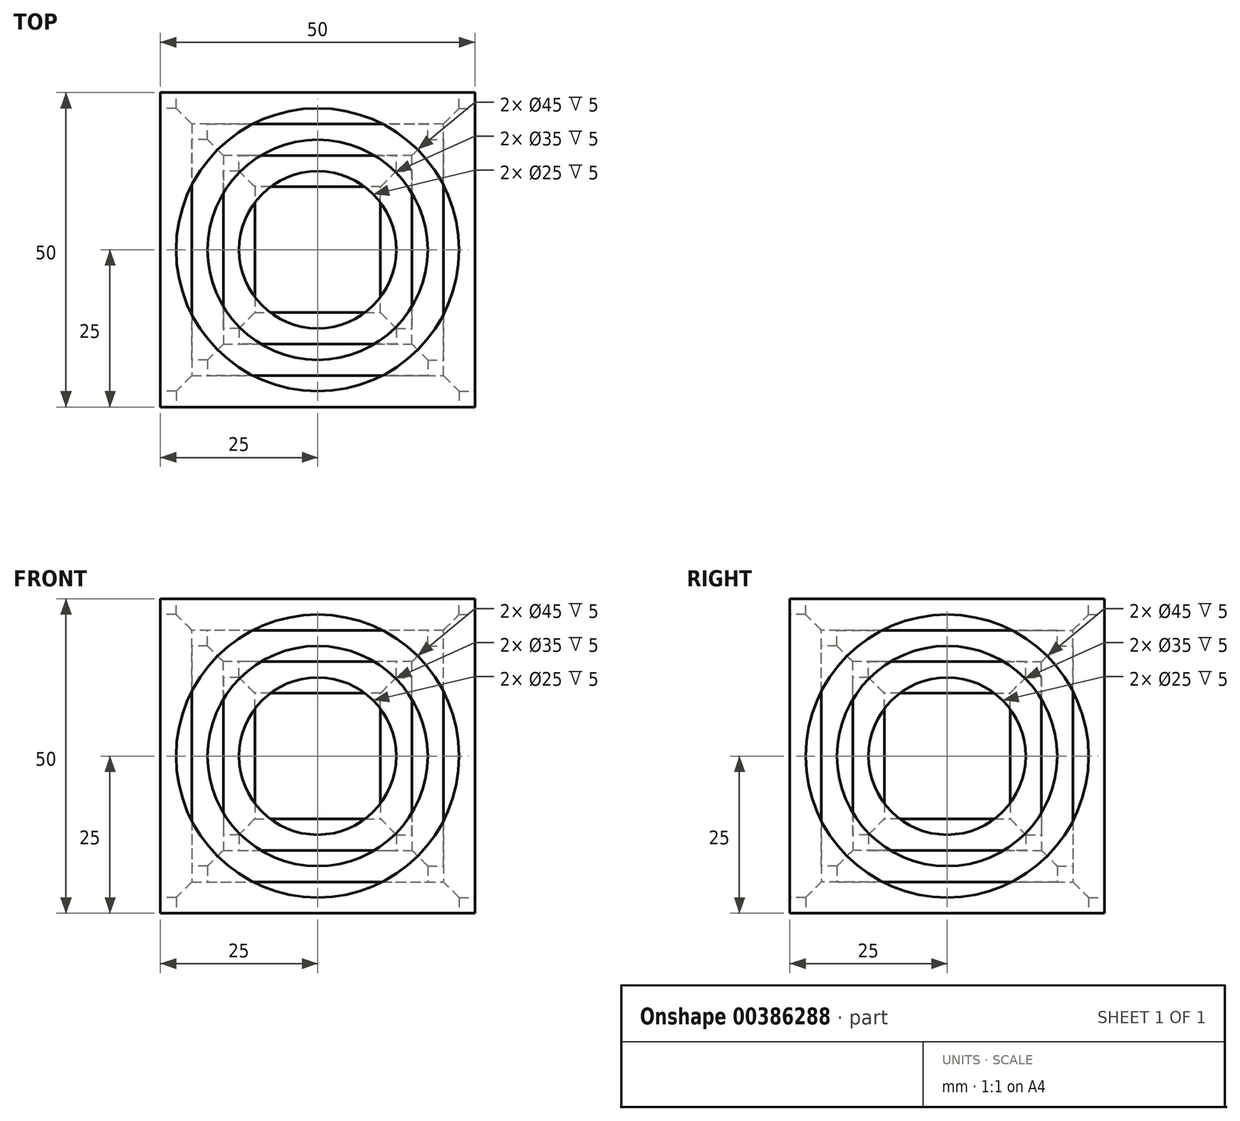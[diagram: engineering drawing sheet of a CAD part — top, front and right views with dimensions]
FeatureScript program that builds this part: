
annotation { "Feature Type Name" : "Feature", "Feature Type Description" : "" }
export const myFeature = defineFeature(function(context is Context, id is Id, definition is map)
    precondition{}
    {
        {
            var Q0;
            Q0=qCreatedBy(makeId("Top.planeOp"),FACE);
            var sketch = newSketch(context, id + "F0", { "sketchPlane" : qUnion([Q0])});
            skLineSegment(sketch, "E0.bottom", {"start": v(0, 0) * mm, "end": v(50, 0) * mm});
            skLineSegment(sketch, "E0.top", {"start": v(0, 50) * mm, "end": v(50, 50) * mm});
            skLineSegment(sketch, "E0.left", {"start": v(0, 0) * mm, "end": v(0, 50) * mm});
            skLineSegment(sketch, "E0.right", {"start": v(50, 0) * mm, "end": v(50, 50) * mm});
            skSolve(sketch);
        }
        {
            var Q0;
            Q0=makeQuery(id+"F0.imprint","IMPRINT",FACE,{"disambiguationData":[TD([[makeQuery(id+"F0.imprint","IMPRINT",EDGE,{"derivedFrom":sQuery(id+"F0.wireOp",EDGE,"E0.bottom")}),1.0]])]});
            extrude(context, id + "F1", {"entities" : qUnion([Q0]), "depth" : 50 * mm});
        }
        {
            var Q0;
            Q0=makeQuery(id+"F1.opExtrude","CAP_FACE",FACE,{"disambiguationData":[OSD([sQuery(id+"F0.wireOp",EDGE,"E0.bottom"),sQuery(id+"F0.wireOp",EDGE,"E0.top"),sQuery(id+"F0.wireOp",EDGE,"E0.left"),sQuery(id+"F0.wireOp",EDGE,"E0.right")])],"isStart":false});
            var sketch = newSketch(context, id + "F2", { "sketchPlane" : qUnion([Q0])});
            skCircle(sketch, "E1", {"center": v(25, 25) * mm, "radius": 22.5 * mm});
            skPoint(sketch, "E1.centerSnap0", {"position": v(50, 25) * mm});
            skPoint(sketch, "E1.centerSnap1", {"position": v(25, 50) * mm});
            skSolve(sketch);
        }
        {
            var Q0;
            Q0=makeQuery(id+"F2.imprint","IMPRINT",FACE,{"disambiguationData":[TD([[makeQuery(id+"F2.imprint","IMPRINT",EDGE,{"derivedFrom":sQuery(id+"F2.wireOp",EDGE,"E1")}),1.0]])]});
            extrude(context, id + "F3", {"entities" : qUnion([Q0]), "operationType" : NewBodyOperationType.REMOVE, "oppositeDirection" : true, "depth" : 5 * mm});
        }
        {
            var Q0;
            Q0=makeQuery(id+"F3.boolean.opBoolean","COPY",FACE,{"derivedFrom":makeQuery(id+"F3.opExtrude","CAP_FACE",FACE,{"disambiguationData":[OSD([sQuery(id+"F2.wireOp",EDGE,"E1")])],"isStart":false})});
            var sketch = newSketch(context, id + "F4", { "sketchPlane" : qUnion([Q0])});
            skCircle(sketch, "E2", {"center": v(25, 25) * mm, "radius": 17.5 * mm});
            skSolve(sketch);
        }
        {
            var Q0;
            Q0=makeQuery(id+"F4.imprint","IMPRINT",FACE,{"disambiguationData":[TD([[makeQuery(id+"F4.imprint","IMPRINT",EDGE,{"derivedFrom":sQuery(id+"F4.wireOp",EDGE,"E2")}),1.0]])]});
            extrude(context, id + "F5", {"entities" : qUnion([Q0]), "operationType" : NewBodyOperationType.REMOVE, "oppositeDirection" : true, "depth" : 5 * mm});
        }
        {
            var Q0;
            Q0=makeQuery(id+"F5.boolean.opBoolean","COPY",FACE,{"derivedFrom":makeQuery(id+"F5.opExtrude","CAP_FACE",FACE,{"disambiguationData":[OSD([sQuery(id+"F4.wireOp",EDGE,"E2")])],"isStart":false})});
            var sketch = newSketch(context, id + "F6", { "sketchPlane" : qUnion([Q0])});
            skCircle(sketch, "E3", {"center": v(25, 25) * mm, "radius": 12.5 * mm});
            skSolve(sketch);
        }
        {
            var Q0;
            Q0 = qSketchRegion(id + "F6", true);
            extrude(context, id + "F7", {"entities" : qUnion([Q0]), "operationType" : NewBodyOperationType.REMOVE, "oppositeDirection" : true, "depth" : 5 * mm});
        }
        {
            var Q0;
            Q0=makeQuery(id+"F1.opExtrude","SWEPT_FACE",FACE,{"disambiguationData":[OSD([sQuery(id+"F0.wireOp",EDGE,"E0.left")])]});
            var sketch = newSketch(context, id + "F8", { "sketchPlane" : qUnion([Q0])});
            skCircle(sketch, "E4", {"center": v(-25, 25) * mm, "radius": 22.5 * mm});
            skPoint(sketch, "E4.centerSnap0", {"position": v(-25, 50) * mm});
            skPoint(sketch, "E4.centerSnap1", {"position": v(-50, 25) * mm});
            skSolve(sketch);
        }
        {
            var Q0;
            Q0=makeQuery(id+"F8.imprint","IMPRINT",FACE,{"disambiguationData":[TD([[makeQuery(id+"F8.imprint","IMPRINT",EDGE,{"derivedFrom":sQuery(id+"F8.wireOp",EDGE,"E4")}),1.0]])]});
            extrude(context, id + "F9", {"entities" : qUnion([Q0]), "operationType" : NewBodyOperationType.REMOVE, "oppositeDirection" : true, "depth" : 5 * mm});
        }
        {
            var Q0;
            Q0=makeQuery(id+"F9.boolean.opBoolean","COPY",FACE,{"derivedFrom":makeQuery(id+"F9.opExtrude","CAP_FACE",FACE,{"disambiguationData":[OSD([sQuery(id+"F8.wireOp",EDGE,"E4")])],"isStart":false})});
            var sketch = newSketch(context, id + "F10", { "sketchPlane" : qUnion([Q0])});
            skCircle(sketch, "E5", {"center": v(-25, 25) * mm, "radius": 17.5 * mm});
            skSolve(sketch);
        }
        {
            var Q0;
            Q0 = qSketchRegion(id + "F10", true);
            var Q1;
            Q1=makeQuery(id+"F10.imprint","IMPRINT",FACE,{"disambiguationData":[TD([[makeQuery(id+"F10.imprint","IMPRINT",EDGE,{"derivedFrom":sQuery(id+"F10.wireOp",EDGE,"E5")}),1.0]])]});
            extrude(context, id + "F11", {"entities" : qUnion([Q0, Q1]), "operationType" : NewBodyOperationType.REMOVE, "oppositeDirection" : true, "depth" : 5 * mm});
        }
        {
            var Q0;
            Q0=makeQuery(id+"F11.boolean.opBoolean","COPY",FACE,{"derivedFrom":makeQuery(id+"F11.opExtrude","CAP_FACE",FACE,{"disambiguationData":[OSD([sQuery(id+"F10.wireOp",EDGE,"E5")])],"isStart":false})});
            var sketch = newSketch(context, id + "F12", { "sketchPlane" : qUnion([Q0])});
            skCircle(sketch, "E6", {"center": v(-25, 25) * mm, "radius": 12.5 * mm});
            skSolve(sketch);
        }
        {
            var Q0;
            Q0 = qSketchRegion(id + "F12", true);
            extrude(context, id + "F13", {"entities" : qUnion([Q0]), "operationType" : NewBodyOperationType.REMOVE, "oppositeDirection" : true, "depth" : 5 * mm});
        }
        {
            var Q0;
            Q0=makeQuery(id+"F1.opExtrude","SWEPT_FACE",FACE,{"disambiguationData":[OSD([sQuery(id+"F0.wireOp",EDGE,"E0.bottom")])]});
            var sketch = newSketch(context, id + "F14", { "sketchPlane" : qUnion([Q0])});
            skCircle(sketch, "E7", {"center": v(25, 25) * mm, "radius": 22.5 * mm});
            skPoint(sketch, "E7.centerSnap0", {"position": v(50, 25) * mm});
            skPoint(sketch, "E7.centerSnap1", {"position": v(25, 50) * mm});
            skSolve(sketch);
        }
        {
            var Q0;
            Q0=makeQuery(id+"F14.imprint","IMPRINT",FACE,{"disambiguationData":[TD([[makeQuery(id+"F14.imprint","IMPRINT",EDGE,{"derivedFrom":sQuery(id+"F14.wireOp",EDGE,"E7")}),1.0]])]});
            extrude(context, id + "F15", {"entities" : qUnion([Q0]), "operationType" : NewBodyOperationType.REMOVE, "oppositeDirection" : true, "depth" : 5 * mm});
        }
        {
            var Q0;
            Q0=makeQuery(id+"F15.boolean.opBoolean","COPY",FACE,{"derivedFrom":makeQuery(id+"F15.opExtrude","CAP_FACE",FACE,{"disambiguationData":[OSD([sQuery(id+"F14.wireOp",EDGE,"E7")])],"isStart":false})});
            var sketch = newSketch(context, id + "F16", { "sketchPlane" : qUnion([Q0])});
            skCircle(sketch, "E8", {"center": v(25, 25) * mm, "radius": 17.5 * mm});
            skSolve(sketch);
        }
        {
            var Q0;
            Q0 = qSketchRegion(id + "F16", true);
            extrude(context, id + "F17", {"entities" : qUnion([Q0]), "operationType" : NewBodyOperationType.REMOVE, "oppositeDirection" : true, "depth" : 5 * mm});
        }
        {
            var Q0;
            Q0=makeQuery(id+"F17.boolean.opBoolean","COPY",FACE,{"derivedFrom":makeQuery(id+"F17.opExtrude","CAP_FACE",FACE,{"disambiguationData":[OSD([sQuery(id+"F16.wireOp",EDGE,"E8")])],"isStart":false})});
            var sketch = newSketch(context, id + "F18", { "sketchPlane" : qUnion([Q0])});
            skCircle(sketch, "E9", {"center": v(25, 25) * mm, "radius": 12.5 * mm});
            skSolve(sketch);
        }
        {
            var Q0;
            Q0 = qSketchRegion(id + "F18", true);
            extrude(context, id + "F19", {"entities" : qUnion([Q0]), "operationType" : NewBodyOperationType.REMOVE, "oppositeDirection" : true, "depth" : 5 * mm});
        }
        {
            var Q0;
            Q0=makeQuery(id+"F1.opExtrude","SWEPT_FACE",FACE,{"disambiguationData":[OSD([sQuery(id+"F0.wireOp",EDGE,"E0.right")])]});
            var sketch = newSketch(context, id + "F20", { "sketchPlane" : qUnion([Q0])});
            skCircle(sketch, "E10", {"center": v(25, 25) * mm, "radius": 22.5 * mm});
            skPoint(sketch, "E10.centerSnap0", {"position": v(25, 0) * mm});
            skPoint(sketch, "E10.centerSnap1", {"position": v(50, 25) * mm});
            skSolve(sketch);
        }
        {
            var Q0;
            Q0 = qSketchRegion(id + "F20", true);
            extrude(context, id + "F21", {"entities" : qUnion([Q0]), "operationType" : NewBodyOperationType.REMOVE, "oppositeDirection" : true, "depth" : 5 * mm});
        }
        {
            var Q0;
            Q0=makeQuery(id+"F21.boolean.opBoolean","COPY",FACE,{"derivedFrom":makeQuery(id+"F21.opExtrude","CAP_FACE",FACE,{"disambiguationData":[OSD([sQuery(id+"F20.wireOp",EDGE,"E10")])],"isStart":false})});
            var sketch = newSketch(context, id + "F22", { "sketchPlane" : qUnion([Q0])});
            skCircle(sketch, "E11", {"center": v(25, 25) * mm, "radius": 17.5 * mm});
            skSolve(sketch);
        }
        {
            var Q0;
            Q0 = qSketchRegion(id + "F22", true);
            extrude(context, id + "F23", {"entities" : qUnion([Q0]), "operationType" : NewBodyOperationType.REMOVE, "oppositeDirection" : true, "depth" : 5 * mm});
        }
        {
            var Q0;
            Q0=makeQuery(id+"F23.boolean.opBoolean","COPY",FACE,{"derivedFrom":makeQuery(id+"F23.opExtrude","CAP_FACE",FACE,{"disambiguationData":[OSD([sQuery(id+"F22.wireOp",EDGE,"E11")])],"isStart":false})});
            var sketch = newSketch(context, id + "F24", { "sketchPlane" : qUnion([Q0])});
            skCircle(sketch, "E12", {"center": v(25, 25) * mm, "radius": 12.5 * mm});
            skSolve(sketch);
        }
        {
            var Q0;
            Q0 = qSketchRegion(id + "F24", true);
            extrude(context, id + "F25", {"entities" : qUnion([Q0]), "operationType" : NewBodyOperationType.REMOVE, "oppositeDirection" : true, "depth" : 5 * mm});
        }
        {
            var Q0;
            Q0=makeQuery(id+"F1.opExtrude","SWEPT_FACE",FACE,{"disambiguationData":[OSD([sQuery(id+"F0.wireOp",EDGE,"E0.top")])]});
            var sketch = newSketch(context, id + "F26", { "sketchPlane" : qUnion([Q0])});
            skCircle(sketch, "E13", {"center": v(-25, 25) * mm, "radius": 22.5 * mm});
            skPoint(sketch, "E13.centerSnap0", {"position": v(0, 25) * mm});
            skPoint(sketch, "E13.centerSnap1", {"position": v(-25, 50) * mm});
            skSolve(sketch);
        }
        {
            var Q0;
            Q0 = qSketchRegion(id + "F26", true);
            extrude(context, id + "F27", {"entities" : qUnion([Q0]), "operationType" : NewBodyOperationType.REMOVE, "oppositeDirection" : true, "depth" : 5 * mm});
        }
        {
            var Q0;
            Q0=makeQuery(id+"F27.boolean.opBoolean","COPY",FACE,{"derivedFrom":makeQuery(id+"F27.opExtrude","CAP_FACE",FACE,{"disambiguationData":[OSD([sQuery(id+"F26.wireOp",EDGE,"E13")])],"isStart":false})});
            var sketch = newSketch(context, id + "F28", { "sketchPlane" : qUnion([Q0])});
            skCircle(sketch, "E14", {"center": v(-25, 25) * mm, "radius": 17.5 * mm});
            skSolve(sketch);
        }
        {
            var Q0;
            Q0 = qSketchRegion(id + "F28", true);
            extrude(context, id + "F29", {"entities" : qUnion([Q0]), "operationType" : NewBodyOperationType.REMOVE, "oppositeDirection" : true, "depth" : 5 * mm});
        }
        {
            var Q0;
            Q0=makeQuery(id+"F29.boolean.opBoolean","COPY",FACE,{"derivedFrom":makeQuery(id+"F29.opExtrude","CAP_FACE",FACE,{"disambiguationData":[OSD([sQuery(id+"F28.wireOp",EDGE,"E14")])],"isStart":false})});
            var sketch = newSketch(context, id + "F30", { "sketchPlane" : qUnion([Q0])});
            skCircle(sketch, "E15", {"center": v(-25, 25) * mm, "radius": 12.5 * mm});
            skSolve(sketch);
        }
        {
            var Q0;
            Q0 = qSketchRegion(id + "F30", true);
            extrude(context, id + "F31", {"entities" : qUnion([Q0]), "operationType" : NewBodyOperationType.REMOVE, "oppositeDirection" : true, "depth" : 5 * mm});
        }
        {
            var Q0;
            Q0=makeQuery(id+"F1.opExtrude","CAP_FACE",FACE,{"disambiguationData":[OSD([sQuery(id+"F0.wireOp",EDGE,"E0.bottom"),sQuery(id+"F0.wireOp",EDGE,"E0.top"),sQuery(id+"F0.wireOp",EDGE,"E0.left"),sQuery(id+"F0.wireOp",EDGE,"E0.right")])],"isStart":true});
            var sketch = newSketch(context, id + "F32", { "sketchPlane" : qUnion([Q0])});
            skCircle(sketch, "E16", {"center": v(25, -25) * mm, "radius": 22.5 * mm});
            skPoint(sketch, "E16.centerSnap0", {"position": v(25, 0) * mm});
            skPoint(sketch, "E16.centerSnap1", {"position": v(50, -25) * mm});
            skSolve(sketch);
        }
        {
            var Q0;
            Q0=makeQuery(id+"F32.imprint","IMPRINT",FACE,{"disambiguationData":[TD([[makeQuery(id+"F32.imprint","IMPRINT",EDGE,{"derivedFrom":sQuery(id+"F32.wireOp",EDGE,"E16")}),1.0]])]});
            var Q1;
            Q1 = qSketchRegion(id + "F32", true);
            extrude(context, id + "F33", {"entities" : qUnion([Q0, Q1]), "operationType" : NewBodyOperationType.REMOVE, "oppositeDirection" : true, "depth" : 5 * mm});
        }
        {
            var Q0;
            Q0=makeQuery(id+"F33.boolean.opBoolean","COPY",FACE,{"derivedFrom":makeQuery(id+"F33.opExtrude","CAP_FACE",FACE,{"disambiguationData":[OSD([sQuery(id+"F32.wireOp",EDGE,"E16")])],"isStart":false})});
            var sketch = newSketch(context, id + "F34", { "sketchPlane" : qUnion([Q0])});
            skCircle(sketch, "E17", {"center": v(25, -25) * mm, "radius": 17.5 * mm});
            skSolve(sketch);
        }
        {
            var Q0;
            Q0 = qSketchRegion(id + "F34", true);
            extrude(context, id + "F35", {"entities" : qUnion([Q0]), "operationType" : NewBodyOperationType.REMOVE, "oppositeDirection" : true, "depth" : 5 * mm});
        }
        {
            var Q0;
            Q0=makeQuery(id+"F35.boolean.opBoolean","COPY",FACE,{"derivedFrom":makeQuery(id+"F35.opExtrude","CAP_FACE",FACE,{"disambiguationData":[OSD([sQuery(id+"F34.wireOp",EDGE,"E17")])],"isStart":false})});
            var sketch = newSketch(context, id + "F36", { "sketchPlane" : qUnion([Q0])});
            skCircle(sketch, "E18", {"center": v(25, -25) * mm, "radius": 12.5 * mm});
            skSolve(sketch);
        }
        {
            var Q0;
            Q0 = qSketchRegion(id + "F36", true);
            extrude(context, id + "F37", {"entities" : qUnion([Q0]), "operationType" : NewBodyOperationType.REMOVE, "oppositeDirection" : true, "depth" : 5 * mm});
        }
    });
